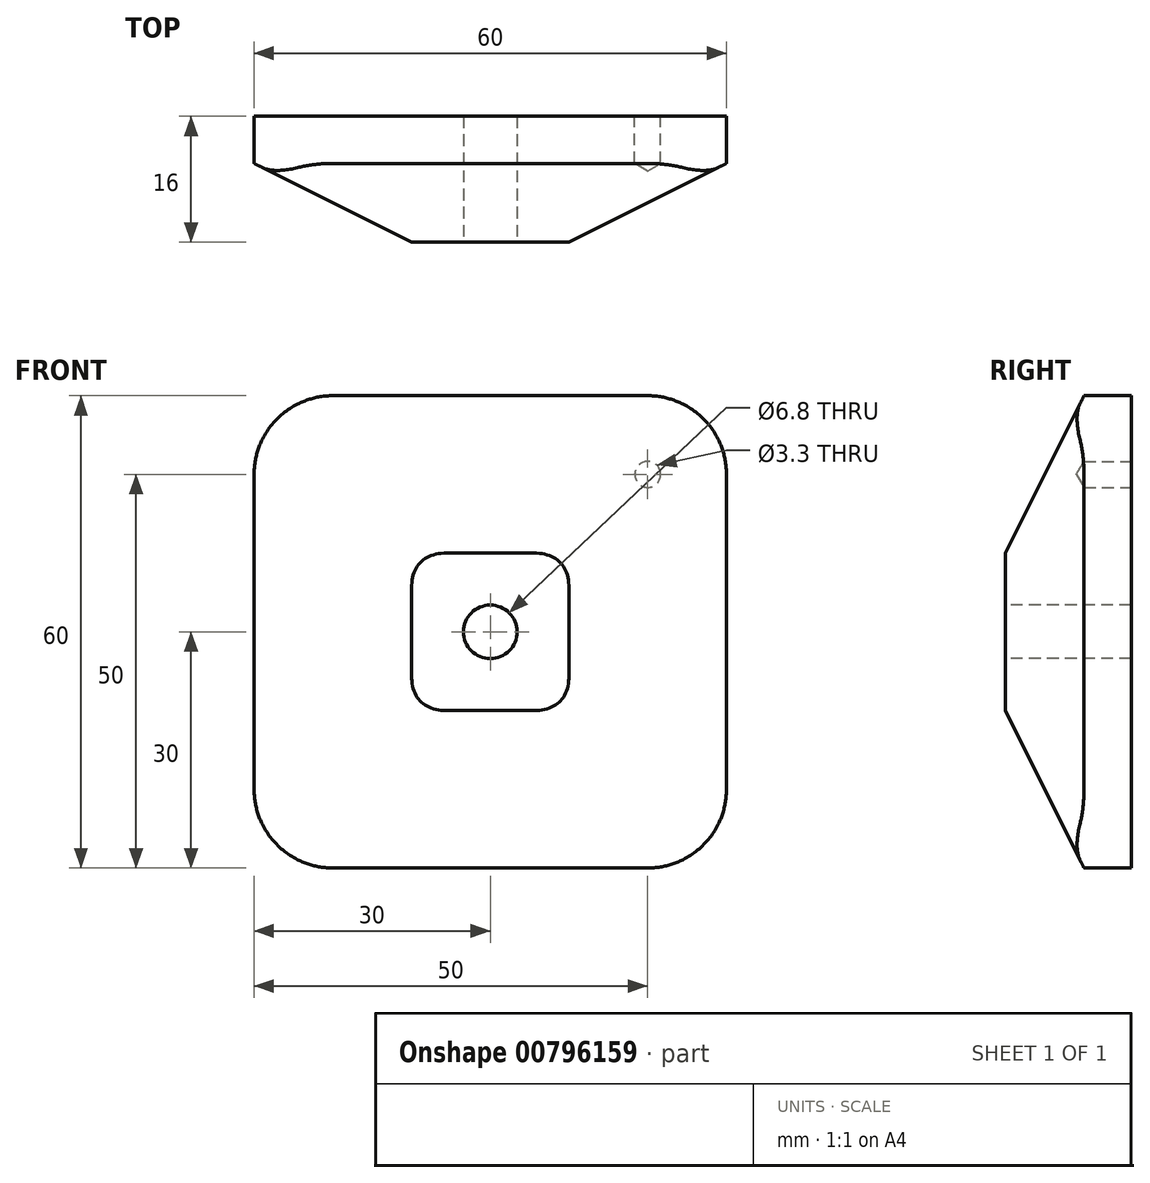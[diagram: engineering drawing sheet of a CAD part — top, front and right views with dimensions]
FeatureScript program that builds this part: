
annotation { "Feature Type Name" : "Feature", "Feature Type Description" : "" }
export const myFeature = defineFeature(function(context is Context, id is Id, definition is map)
    precondition{}
    {
        {
            var Q0;
            Q0=qCreatedBy(makeId("Front.planeOp"),FACE);
            var sketch = newSketch(context, id + "F0", { "sketchPlane" : qUnion([Q0])});
            skLineSegment(sketch, "E0", {"start": v(0, 66.93) * mm, "end": v(0, -21.07) * mm, "construction": true});
            skLineSegment(sketch, "E1.bottom", {"start": v(-30, 30) * mm, "end": v(30, 30) * mm});
            skLineSegment(sketch, "E1.top", {"start": v(-30, -30) * mm, "end": v(30, -30) * mm});
            skLineSegment(sketch, "E1.left", {"start": v(-30, 30) * mm, "end": v(-30, -30) * mm});
            skLineSegment(sketch, "E1.right", {"start": v(30, 30) * mm, "end": v(30, -30) * mm});
            skSolve(sketch);
        }
        {
            var Q0;
            Q0=makeQuery(id+"F0.imprint","IMPRINT",FACE,{"disambiguationData":[TD([[makeQuery(id+"F0.imprint","IMPRINT",EDGE,{"derivedFrom":sQuery(id+"F0.wireOp",EDGE,"E1.bottom")}),-1.0]])]});
            extrude(context, id + "F1", {"entities" : qUnion([Q0]), "depth" : 16 * mm, "offsetDistance" : 25 * mm});
        }
        {
            var Q0;
            Q0=makeQuery(id+"F1.opExtrude","CAP_EDGE",EDGE,{"disambiguationData":[OSD([sQuery(id+"F0.wireOp",EDGE,"E1.top")])],"isStart":false});
            var Q1;
            Q1=makeQuery(id+"F1.opExtrude","CAP_EDGE",EDGE,{"disambiguationData":[OSD([sQuery(id+"F0.wireOp",EDGE,"E1.right")])],"isStart":false});
            var Q2;
            Q2=makeQuery(id+"F1.opExtrude","CAP_EDGE",EDGE,{"disambiguationData":[OSD([sQuery(id+"F0.wireOp",EDGE,"E1.bottom")])],"isStart":false});
            var Q3;
            Q3=makeQuery(id+"F1.opExtrude","CAP_EDGE",EDGE,{"disambiguationData":[OSD([sQuery(id+"F0.wireOp",EDGE,"E1.left")])],"isStart":false});
            chamfer(context, id + "F2", {"entities" : qUnion([Q0, Q1, Q2, Q3]), "chamferType" : ChamferType.TWO_OFFSETS, "width1" : 20 * mm, "oppositeDirection" : false, "width2" : 10 * mm, "tangentPropagation" : true});
        }
        {
            var Q0;
            Q0=makeQuery(id+"F2.opChamfer","BLEND_EDGE",EDGE,{"blendedFrom":[makeQuery(id+"F1.opExtrude","CAP_EDGE",EDGE,{"disambiguationData":[OSD([sQuery(id+"F0.wireOp",EDGE,"E1.top")])],"isStart":false}),makeQuery(id+"F1.opExtrude","CAP_EDGE",EDGE,{"disambiguationData":[OSD([sQuery(id+"F0.wireOp",EDGE,"E1.right")])],"isStart":false})],"blendedInto":[]});
            var Q1;
            Q1=makeQuery(id+"F2.opChamfer","BLEND_EDGE",EDGE,{"blendedFrom":[makeQuery(id+"F1.opExtrude","CAP_EDGE",EDGE,{"disambiguationData":[OSD([sQuery(id+"F0.wireOp",EDGE,"E1.bottom")])],"isStart":false}),makeQuery(id+"F1.opExtrude","CAP_EDGE",EDGE,{"disambiguationData":[OSD([sQuery(id+"F0.wireOp",EDGE,"E1.right")])],"isStart":false})],"blendedInto":[]});
            var Q2;
            Q2=makeQuery(id+"F2.opChamfer","BLEND_EDGE",EDGE,{"blendedFrom":[makeQuery(id+"F1.opExtrude","CAP_EDGE",EDGE,{"disambiguationData":[OSD([sQuery(id+"F0.wireOp",EDGE,"E1.top")])],"isStart":false}),makeQuery(id+"F1.opExtrude","CAP_EDGE",EDGE,{"disambiguationData":[OSD([sQuery(id+"F0.wireOp",EDGE,"E1.left")])],"isStart":false})],"blendedInto":[]});
            var Q3;
            Q3=makeQuery(id+"F2.opChamfer","BLEND_EDGE",EDGE,{"blendedFrom":[makeQuery(id+"F1.opExtrude","CAP_EDGE",EDGE,{"disambiguationData":[OSD([sQuery(id+"F0.wireOp",EDGE,"E1.bottom")])],"isStart":false}),makeQuery(id+"F1.opExtrude","CAP_EDGE",EDGE,{"disambiguationData":[OSD([sQuery(id+"F0.wireOp",EDGE,"E1.left")])],"isStart":false})],"blendedInto":[]});
            var Q4;
            Q4=makeQuery(id+"F1.opExtrude","SWEPT_EDGE",EDGE,{"disambiguationData":[OSD([sQuery(id+"F0.wireOp",EDGE,"E1.top"),sQuery(id+"F0.wireOp",EDGE,"E1.right")])]});
            var Q5;
            Q5=makeQuery(id+"F1.opExtrude","SWEPT_EDGE",EDGE,{"disambiguationData":[OSD([sQuery(id+"F0.wireOp",EDGE,"E1.bottom"),sQuery(id+"F0.wireOp",EDGE,"E1.right")])]});
            var Q6;
            Q6=makeQuery(id+"F1.opExtrude","SWEPT_EDGE",EDGE,{"disambiguationData":[OSD([sQuery(id+"F0.wireOp",EDGE,"E1.top"),sQuery(id+"F0.wireOp",EDGE,"E1.left")])]});
            var Q7;
            Q7=makeQuery(id+"F1.opExtrude","SWEPT_EDGE",EDGE,{"disambiguationData":[OSD([sQuery(id+"F0.wireOp",EDGE,"E1.bottom"),sQuery(id+"F0.wireOp",EDGE,"E1.left")])]});
            fillet(context, id + "F3", {"entities" : qUnion([Q0, Q1, Q2, Q3, Q4, Q5, Q6, Q7]), "radius" : 10 * mm, "tangentPropagation" : true, "allowEdgeOverflow" : false});
        }
        {
            var Q0;
            Q0=makeQuery(id+"F1.opExtrude","CAP_FACE",FACE,{"disambiguationData":[OSD([sQuery(id+"F0.wireOp",EDGE,"E1.bottom"),sQuery(id+"F0.wireOp",EDGE,"E1.top"),sQuery(id+"F0.wireOp",EDGE,"E1.left"),sQuery(id+"F0.wireOp",EDGE,"E1.right")])],"isStart":false});
            var sketch = newSketch(context, id + "F4", { "sketchPlane" : qUnion([Q0])});
            skPoint(sketch, "E2", {"position": v(0, 0) * mm});
            skSolve(sketch);
        }
        {
            var Q0;
            Q0=sQuery(id+"F4.wireOp",VERTEX,"E2");
            var Q1;
            Q1=makeQuery(id+"F1.opExtrude","SWEPT_BODY",BODY,{"disambiguationData":[OSD([sQuery(id+"F0.wireOp",EDGE,"E1.bottom"),sQuery(id+"F0.wireOp",EDGE,"E1.top"),sQuery(id+"F0.wireOp",EDGE,"E1.left"),sQuery(id+"F0.wireOp",EDGE,"E1.right")])]});
            hole(context, id + "F5", {"style" : HoleStyle.SIMPLE, "endStyle" : HoleEndStyle.THROUGH, "standardTappedOrClearance" : lookupTablePath({ "standard" : "ISO", "engagement" : "75%", "pitch" : "1.25 mm", "size" : "M8", "type" : "Tapped" }), "standardBlindInLast" : lookupTablePath({ "standard" : "ISO", "engagement" : "75%", "pitch" : "1.25 mm", "size" : "M8", "type" : "Tapped" }), "holeDiameter" : 6.8 * mm, "majorDiameter" : 8 * mm, "showTappedDepth" : true, "isTappedThrough" : true, "tappedDepth" : 16.25 * mm, "tapClearance" : 3, "startFromSketch" : true, "locations" : qUnion([Q0]), "scope" : qUnion([Q1])});
        }
        {
            var Q0;
            Q0=makeQuery(id+"F1.opExtrude","CAP_FACE",FACE,{"disambiguationData":[OSD([sQuery(id+"F0.wireOp",EDGE,"E1.bottom"),sQuery(id+"F0.wireOp",EDGE,"E1.top"),sQuery(id+"F0.wireOp",EDGE,"E1.left"),sQuery(id+"F0.wireOp",EDGE,"E1.right")])],"isStart":true});
            var sketch = newSketch(context, id + "F6", { "sketchPlane" : qUnion([Q0])});
            skPoint(sketch, "E3", {"position": v(-20, 20) * mm});
            skSolve(sketch);
        }
        {
            var Q0;
            Q0=sQuery(id+"F6.wireOp",VERTEX,"E3");
            var Q1;
            Q1=makeQuery(id+"F1.opExtrude","SWEPT_BODY",BODY,{"disambiguationData":[OSD([sQuery(id+"F0.wireOp",EDGE,"E1.bottom"),sQuery(id+"F0.wireOp",EDGE,"E1.top"),sQuery(id+"F0.wireOp",EDGE,"E1.left"),sQuery(id+"F0.wireOp",EDGE,"E1.right")])]});
            hole(context, id + "F7", {"style" : HoleStyle.SIMPLE, "endStyle" : HoleEndStyle.BLIND, "standardTappedOrClearance" : lookupTablePath({ "standard" : "ISO", "engagement" : "75%", "pitch" : "0.7 mm", "size" : "M4", "type" : "Tapped" }), "standardBlindInLast" : lookupTablePath({ "standard" : "ISO", "engagement" : "75%", "pitch" : "0.7 mm", "size" : "M4", "type" : "Tapped" }), "holeDiameter" : 3.3 * mm, "majorDiameter" : 4 * mm, "showTappedDepth" : true, "holeDepth" : 6 * mm, "isTappedThrough" : true, "tappedDepth" : 3.9 * mm, "tapClearance" : 3, "startFromSketch" : true, "locations" : qUnion([Q0]), "scope" : qUnion([Q1])});
        }
    });
